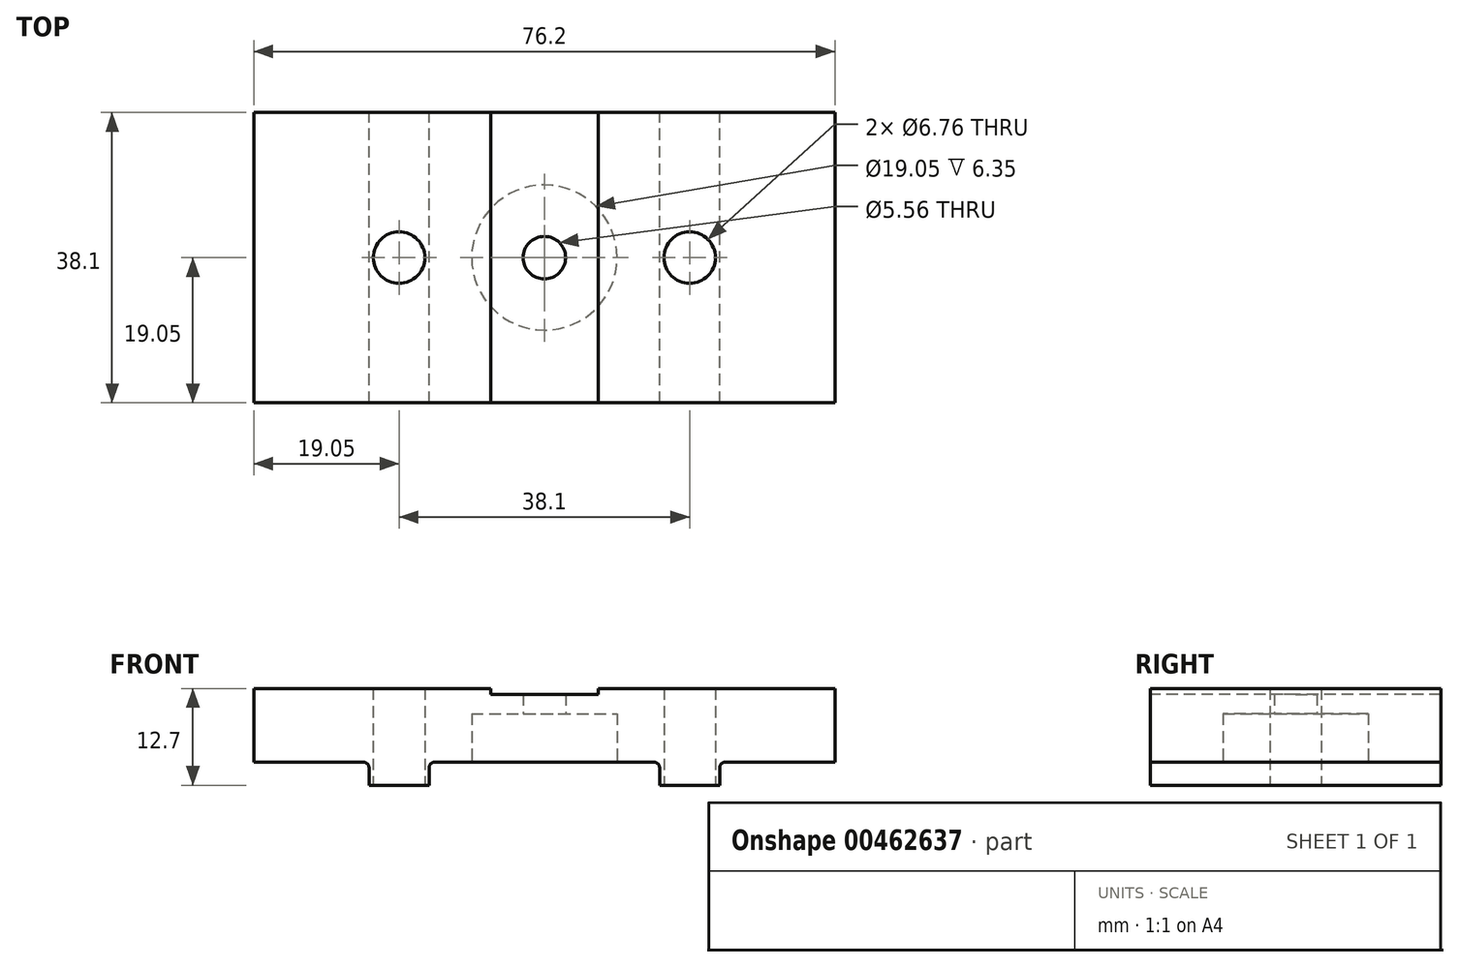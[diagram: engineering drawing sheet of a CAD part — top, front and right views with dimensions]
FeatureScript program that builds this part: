
annotation { "Feature Type Name" : "Feature", "Feature Type Description" : "" }
export const myFeature = defineFeature(function(context is Context, id is Id, definition is map)
    precondition{}
    {
        {
            var Q0;
            Q0=qCreatedBy(makeId("Top.planeOp"),FACE);
            var sketch = newSketch(context, id + "F0", { "sketchPlane" : qUnion([Q0])});
            skLineSegment(sketch, "E0", {"start": v(0, 0) * mm, "end": v(0, -38.1) * mm});
            skLineSegment(sketch, "E1", {"start": v(76.2, -38.1) * mm, "end": v(0, -38.1) * mm});
            skLineSegment(sketch, "E2", {"start": v(76.2, -38.1) * mm, "end": v(76.2, 0) * mm});
            skLineSegment(sketch, "E3", {"start": v(0, 0) * mm, "end": v(76.2, 0) * mm});
            skSolve(sketch);
        }
        {
            var Q0;
            Q0=makeQuery(id+"F0.imprint","IMPRINT",FACE,{"disambiguationData":[TD([[makeQuery(id+"F0.imprint","IMPRINT",EDGE,{"derivedFrom":sQuery(id+"F0.wireOp",EDGE,"E0")}),1.0]])]});
            extrude(context, id + "F1", {"entities" : qUnion([Q0]), "oppositeDirection" : true, "depth" : 12.7 * mm});
        }
        {
            var Q0;
            Q0=makeQuery(id+"F1.opExtrude","CAP_FACE",FACE,{"disambiguationData":[OSD([sQuery(id+"F0.wireOp",EDGE,"E0"),sQuery(id+"F0.wireOp",EDGE,"E1"),sQuery(id+"F0.wireOp",EDGE,"E2"),sQuery(id+"F0.wireOp",EDGE,"E3")])],"isStart":true});
            var sketch = newSketch(context, id + "F2", { "sketchPlane" : qUnion([Q0])});
            skLineSegment(sketch, "E4", {"start": v(31.06, 0) * mm, "end": v(31.06, -38.1) * mm});
            skLineSegment(sketch, "E5", {"start": v(45.16, 0) * mm, "end": v(45.16, -38.1) * mm});
            skLineSegment(sketch, "E6", {"start": v(45.16, -38.1) * mm, "end": v(31.06, -38.1) * mm});
            skLineSegment(sketch, "E7", {"start": v(45.16, 0) * mm, "end": v(31.06, 0) * mm});
            skSolve(sketch);
        }
        {
            var Q0;
            Q0=makeQuery(id+"F2.imprint","IMPRINT",FACE,{"disambiguationData":[TD([[makeQuery(id+"F2.imprint","IMPRINT",EDGE,{"derivedFrom":sQuery(id+"F2.wireOp",EDGE,"E4")}),1.0]])]});
            extrude(context, id + "F3", {"entities" : qUnion([Q0]), "operationType" : NewBodyOperationType.REMOVE, "oppositeDirection" : true, "depth" : 0.76 * mm});
        }
        {
            var Q0;
            Q0=makeQuery(id+"F1.opExtrude","SWEPT_FACE",FACE,{"disambiguationData":[OSD([sQuery(id+"F0.wireOp",EDGE,"E3")])]});
            var sketch = newSketch(context, id + "F4", { "sketchPlane" : qUnion([Q0])});
            skLineSegment(sketch, "E8", {"start": v(0, -9.65) * mm, "end": v(-15.11, -9.65) * mm});
            skLineSegment(sketch, "E9", {"start": v(-15.11, -9.65) * mm, "end": v(-15.11, -12.7) * mm});
            skLineSegment(sketch, "E10", {"start": v(-15.11, -12.7) * mm, "end": v(-22.99, -12.7) * mm});
            skLineSegment(sketch, "E11", {"start": v(-22.99, -12.7) * mm, "end": v(-22.99, -9.65) * mm});
            skLineSegment(sketch, "E12", {"start": v(-22.99, -9.65) * mm, "end": v(-53.21, -9.65) * mm});
            skLineSegment(sketch, "E13", {"start": v(-53.21, -9.65) * mm, "end": v(-53.21, -12.7) * mm});
            skLineSegment(sketch, "E14", {"start": v(-53.21, -12.7) * mm, "end": v(-61.09, -12.7) * mm});
            skLineSegment(sketch, "E15", {"start": v(-61.09, -12.7) * mm, "end": v(-61.09, -9.65) * mm});
            skLineSegment(sketch, "E16", {"start": v(-61.09, -9.65) * mm, "end": v(-76.2, -9.65) * mm});
            skSolve(sketch);
        }
        {
            var Q0;
            {var subQ0=sQuery(id+"F4.wireOp",EDGE,"E15");Q0=makeQuery(id+"F4.imprint","IMPRINT",FACE,{"disambiguationData":[TD([[makeQuery(id+"F4.imprint","IMPRINT",EDGE,{"derivedFrom":subQ0}),1.0]])]});}
            var Q1;
            {var subQ0=sQuery(id+"F4.wireOp",EDGE,"E11");Q1=makeQuery(id+"F4.imprint","IMPRINT",FACE,{"disambiguationData":[TD([[makeQuery(id+"F4.imprint","IMPRINT",EDGE,{"derivedFrom":subQ0}),1.0]])]});}
            var Q2;
            {var subQ0=sQuery(id+"F4.wireOp",EDGE,"E8");Q2=makeQuery(id+"F4.imprint","IMPRINT",FACE,{"disambiguationData":[TD([[makeQuery(id+"F4.imprint","IMPRINT",EDGE,{"derivedFrom":subQ0}),1.0]])]});}
            extrude(context, id + "F5", {"entities" : qUnion([Q0, Q1, Q2]), "operationType" : NewBodyOperationType.REMOVE, "endBound" : BoundingType.THROUGH_ALL, "oppositeDirection" : true, "depth" : 25.4 * mm});
        }
        {
            var Q0;
            Q0=makeQuery(id+"F5.boolean.opBoolean","COPY",FACE,{"derivedFrom":makeQuery(id+"F5.opExtrude","SWEPT_FACE",FACE,{"disambiguationData":[OSD([sQuery(id+"F4.wireOp",EDGE,"E12")])]})});
            var sketch = newSketch(context, id + "F6", { "sketchPlane" : qUnion([Q0])});
            skCircle(sketch, "E17", {"center": v(38.1, 19.05) * mm, "radius": 9.53 * mm});
            skSolve(sketch);
        }
        {
            var Q0;
            Q0=makeQuery(id+"F6.imprint","IMPRINT",FACE,{"disambiguationData":[TD([[makeQuery(id+"F6.imprint","IMPRINT",EDGE,{"derivedFrom":sQuery(id+"F6.wireOp",EDGE,"E17")}),1.0]])]});
            extrude(context, id + "F7", {"entities" : qUnion([Q0]), "operationType" : NewBodyOperationType.REMOVE, "oppositeDirection" : true, "depth" : 6.35 * mm});
        }
        {
            var Q0;
            Q0=makeQuery(id+"F7.boolean.opBoolean","COPY",FACE,{"derivedFrom":makeQuery(id+"F7.opExtrude","CAP_FACE",FACE,{"disambiguationData":[OSD([sQuery(id+"F6.wireOp",EDGE,"E17")])],"isStart":false})});
            var sketch = newSketch(context, id + "F8", { "sketchPlane" : qUnion([Q0])});
            skCircle(sketch, "E18", {"center": v(38.1, 19.05) * mm, "radius": 2.78 * mm});
            skSolve(sketch);
        }
        {
            var Q0;
            Q0=makeQuery(id+"F8.imprint","IMPRINT",FACE,{"disambiguationData":[TD([[makeQuery(id+"F8.imprint","IMPRINT",EDGE,{"derivedFrom":sQuery(id+"F8.wireOp",EDGE,"E18")}),1.0]])]});
            extrude(context, id + "F9", {"entities" : qUnion([Q0]), "operationType" : NewBodyOperationType.REMOVE, "endBound" : BoundingType.THROUGH_ALL, "oppositeDirection" : true, "depth" : 25.4 * mm});
        }
        {
            var Q0;
            {var subQ0=sQuery(id+"F0.wireOp",EDGE,"E1");var subQ1=sQuery(id+"F0.wireOp",EDGE,"E3");Q0=makeQuery(id+"F5.boolean.opBoolean","SPLIT",FACE,{"disambiguationData":[TD([makeQuery(id+"F5.opExtrude","SWEPT_FACE",FACE,{"disambiguationData":[OSD([sQuery(id+"F4.wireOp",EDGE,"E9")])]})])],"derivedFrom":makeQuery(id+"F1.opExtrude","CAP_FACE",FACE,{"disambiguationData":[OSD([sQuery(id+"F0.wireOp",EDGE,"E0"),subQ0,sQuery(id+"F0.wireOp",EDGE,"E2"),subQ1])],"isStart":false})});}
            var sketch = newSketch(context, id + "F10", { "sketchPlane" : qUnion([Q0])});
            skCircle(sketch, "E19", {"center": v(19.05, 19.05) * mm, "radius": 3.38 * mm});
            skCircle(sketch, "E20", {"center": v(57.15, 19.05) * mm, "radius": 3.38 * mm});
            skSolve(sketch);
        }
        {
            var Q0;
            Q0=makeQuery(id+"F10.imprint","IMPRINT",FACE,{"disambiguationData":[TD([[makeQuery(id+"F10.imprint","IMPRINT",EDGE,{"derivedFrom":sQuery(id+"F10.wireOp",EDGE,"E19")}),1.0]])]});
            var Q1;
            Q1=makeQuery(id+"F10.imprint","IMPRINT",FACE,{"disambiguationData":[TD([[makeQuery(id+"F10.imprint","IMPRINT",EDGE,{"derivedFrom":sQuery(id+"F10.wireOp",EDGE,"E20")}),1.0]])]});
            extrude(context, id + "F11", {"entities" : qUnion([Q0, Q1]), "operationType" : NewBodyOperationType.REMOVE, "endBound" : BoundingType.THROUGH_ALL, "oppositeDirection" : true, "depth" : 25.4 * mm});
        }
        {
            var Q0;
            Q0=makeQuery(id+"F5.boolean.opBoolean","COPY",EDGE,{"derivedFrom":makeQuery(id+"F5.opExtrude","SWEPT_EDGE",EDGE,{"disambiguationData":[OSD([sQuery(id+"F4.wireOp",EDGE,"E11"),sQuery(id+"F4.wireOp",EDGE,"E12")])]})});
            var Q1;
            Q1=makeQuery(id+"F5.boolean.opBoolean","COPY",EDGE,{"derivedFrom":makeQuery(id+"F5.opExtrude","SWEPT_EDGE",EDGE,{"disambiguationData":[OSD([sQuery(id+"F4.wireOp",EDGE,"E12"),sQuery(id+"F4.wireOp",EDGE,"E13")])]})});
            var Q2;
            Q2=makeQuery(id+"F5.boolean.opBoolean","COPY",EDGE,{"derivedFrom":makeQuery(id+"F5.opExtrude","SWEPT_EDGE",EDGE,{"disambiguationData":[OSD([sQuery(id+"F4.wireOp",EDGE,"E8"),sQuery(id+"F4.wireOp",EDGE,"E9")])]})});
            var Q3;
            Q3=makeQuery(id+"F5.boolean.opBoolean","COPY",EDGE,{"derivedFrom":makeQuery(id+"F5.opExtrude","SWEPT_EDGE",EDGE,{"disambiguationData":[OSD([sQuery(id+"F4.wireOp",EDGE,"E15"),sQuery(id+"F4.wireOp",EDGE,"E16")])]})});
            fillet(context, id + "F12", {"entities" : qUnion([Q0, Q1, Q2, Q3]), "radius" : 0.76 * mm, "tangentPropagation" : true, "allowEdgeOverflow" : false});
        }
    });
